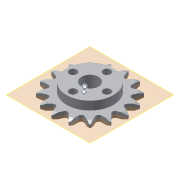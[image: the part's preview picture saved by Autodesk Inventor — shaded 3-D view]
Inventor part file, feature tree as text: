
AUTODESK INVENTOR PART (.ipt)
format: ipt  version: 2013 (Build 170138000, 138)  size: 399,360 bytes
history: native  units: in
note: dims shown in document units (in); Inventor stores cm internally (conversion verified against a paired STEP export)
features: other x13, imported_body x1, plane x1
ambient origin geometry x8: Origin, YZ Plane, XZ Plane, XY Plane, X Axis, Y Axis, Z Axis, Center Point
feature tree (15):
  other  "sprocket_25_16t_tetrix"
  imported_body  "Base1"
  other  "A_1"
  other  "A_2"
  other  "A_4"
  other  "A_5"
  other  "A_6"
  other  "A_3"
  other  "A_7"
  other  "A_8"
  other  "A_9"
  other  "FRONT"
  other  "TOP"
  other  "RIGHT"
  plane  "Work Plane4"
